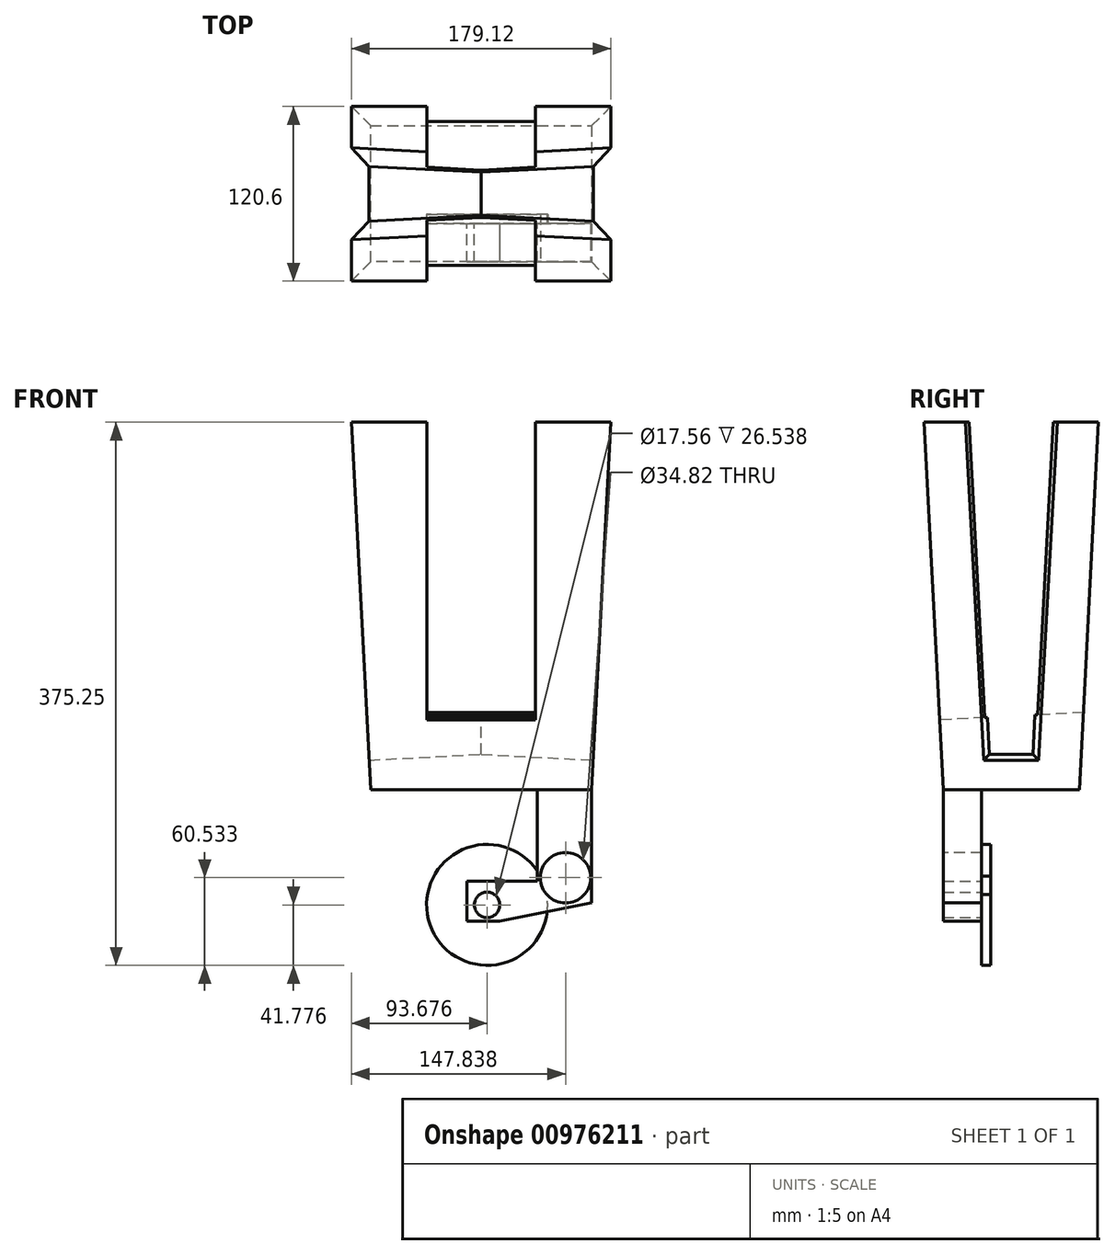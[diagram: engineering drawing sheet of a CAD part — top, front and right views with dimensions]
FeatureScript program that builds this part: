
annotation { "Feature Type Name" : "Feature", "Feature Type Description" : "" }
export const myFeature = defineFeature(function(context is Context, id is Id, definition is map)
    precondition{}
    {
        {
            var Q0;
            Q0=qCreatedBy(makeId("Top.planeOp"),FACE);
            var sketch = newSketch(context, id + "F0", { "sketchPlane" : qUnion([Q0])});
            skLineSegment(sketch, "E0.bottom", {"start": v(76.25, 46.99) * mm, "end": v(-76.25, 46.99) * mm});
            skLineSegment(sketch, "E0.top", {"start": v(76.25, -46.99) * mm, "end": v(-76.25, -46.99) * mm});
            skLineSegment(sketch, "E0.left", {"start": v(76.25, 46.99) * mm, "end": v(76.25, -46.99) * mm});
            skLineSegment(sketch, "E0.right", {"start": v(-76.25, 46.99) * mm, "end": v(-76.25, -46.99) * mm});
            skPoint(sketch, "E0.middle", {"position": v(0, 0) * mm});
            skSolve(sketch);
        }
        {
            var Q0;
            Q0=makeQuery(id+"F0.imprint","IMPRINT",FACE,{"disambiguationData":[TD([[makeQuery(id+"F0.imprint","IMPRINT",EDGE,{"derivedFrom":sQuery(id+"F0.wireOp",EDGE,"E0.bottom")}),1.0]])]});
            extrude(context, id + "F1", {"entities" : qUnion([Q0]), "depth" : 254 * mm, "offsetDistance" : 25.4 * mm, "hasDraft" : true, "draftAngle" : 3 * degree});
        }
        {
            var Q0;
            Q0=qCreatedBy(makeId("Right.planeOp"),FACE);
            var sketch = newSketch(context, id + "F2", { "sketchPlane" : qUnion([Q0])});
            skLineSegment(sketch, "E1", {"start": v(-27.04, 254.5) * mm, "end": v(-14.99, 24.56) * mm});
            skLineSegment(sketch, "E2", {"start": v(-14.99, 24.56) * mm, "end": v(0, 24.56) * mm});
            skLineSegment(sketch, "E3.MirrorCS", {"start": v(27.04, 254.5) * mm, "end": v(14.99, 24.56) * mm});
            skLineSegment(sketch, "E4.MirrorCS", {"start": v(14.99, 24.56) * mm, "end": v(0, 24.56) * mm});
            skLineSegment(sketch, "E5", {"start": v(-27.04, 254.5) * mm, "end": v(27.04, 254.5) * mm});
            skSolve(sketch);
        }
        {
            var Q0;
            Q0 = qSketchRegion(id + "F2", true);
            extrude(context, id + "F3", {"entities" : qUnion([Q0]), "operationType" : NewBodyOperationType.REMOVE, "oppositeDirection" : true, "depth" : 140.97 * mm, "offsetDistance" : 25.4 * mm, "hasDraft" : true, "draftAngle" : 3 * degree, "hasSecondDirection" : true, "secondDirectionOppositeDirection" : false, "secondDirectionDepth" : 247.14 * mm, "hasSecondDirectionDraft" : true, "secondDirectionDraftAngle" : 3 * degree});
        }
        {
            var Q0;
            Q0=makeQuery(id+"F1.opExtrude","SWEPT_FACE",FACE,{"disambiguationData":[OSD([sQuery(id+"F0.wireOp",EDGE,"E0.top")])]});
            var sketch = newSketch(context, id + "F4", { "sketchPlane" : qUnion([Q0])});
            skLineSegment(sketch, "E6", {"start": v(-37.38, 256.8) * mm, "end": v(-37.38, 50.78) * mm});
            skLineSegment(sketch, "E7", {"start": v(-37.38, 50.78) * mm, "end": v(0, 50.78) * mm});
            skLineSegment(sketch, "E8", {"start": v(0, 50.78) * mm, "end": v(0, 256.8) * mm});
            skLineSegment(sketch, "E9", {"start": v(0, 256.8) * mm, "end": v(-37.38, 256.8) * mm});
            skLineSegment(sketch, "E10.MirrorCS", {"start": v(0, 256.8) * mm, "end": v(37.38, 256.8) * mm});
            skLineSegment(sketch, "E11.MirrorCS", {"start": v(37.38, 256.8) * mm, "end": v(37.38, 50.78) * mm});
            skLineSegment(sketch, "E12.MirrorCS", {"start": v(37.38, 50.78) * mm, "end": v(0, 50.78) * mm});
            skSolve(sketch);
        }
        {
            var Q0;
            Q0 = qSketchRegion(id + "F4", true);
            extrude(context, id + "F5", {"entities" : qUnion([Q0]), "operationType" : NewBodyOperationType.REMOVE, "oppositeDirection" : true, "depth" : 149.86 * mm, "offsetDistance" : 25.4 * mm});
        }
        {
            var Q0;
            Q0=makeQuery(id+"F1.opExtrude","CAP_FACE",FACE,{"disambiguationData":[OSD([sQuery(id+"F0.wireOp",EDGE,"E0.bottom"),sQuery(id+"F0.wireOp",EDGE,"E0.top"),sQuery(id+"F0.wireOp",EDGE,"E0.left"),sQuery(id+"F0.wireOp",EDGE,"E0.right")])],"isStart":true});
            var sketch = newSketch(context, id + "F6", { "sketchPlane" : qUnion([Q0])});
            skLineSegment(sketch, "E13.bottom", {"start": v(76.25, 46.99) * mm, "end": v(38.68, 46.99) * mm});
            skLineSegment(sketch, "E13.top", {"start": v(76.25, 20.45) * mm, "end": v(38.68, 20.45) * mm});
            skLineSegment(sketch, "E13.left", {"start": v(76.25, 46.99) * mm, "end": v(76.25, 20.45) * mm});
            skLineSegment(sketch, "E13.right", {"start": v(38.68, 46.99) * mm, "end": v(38.68, 20.45) * mm});
            skSolve(sketch);
        }
        {
            var Q0;
            Q0 = qSketchRegion(id + "F6", true);
            extrude(context, id + "F7", {"entities" : qUnion([Q0]), "operationType" : NewBodyOperationType.ADD, "depth" : 90.68 * mm, "offsetDistance" : 25.4 * mm});
        }
        {
            var Q0;
            Q0=makeQuery(id+"F7.opExtrude","SWEPT_FACE",FACE,{"disambiguationData":[OSD([sQuery(id+"F6.wireOp",EDGE,"E13.right")])]});
            var sketch = newSketch(context, id + "F8", { "sketchPlane" : qUnion([Q0])});
            skLineSegment(sketch, "E14.bottom", {"start": v(46.99, -90.68) * mm, "end": v(20.45, -90.68) * mm});
            skLineSegment(sketch, "E14.top", {"start": v(46.99, -63) * mm, "end": v(20.45, -63) * mm});
            skLineSegment(sketch, "E14.left", {"start": v(46.99, -90.68) * mm, "end": v(46.99, -63) * mm});
            skLineSegment(sketch, "E14.right", {"start": v(20.45, -90.68) * mm, "end": v(20.45, -63) * mm});
            skSolve(sketch);
        }
        {
            var Q0;
            Q0 = qSketchRegion(id + "F8", true);
            extrude(context, id + "F9", {"entities" : qUnion([Q0]), "operationType" : NewBodyOperationType.ADD, "depth" : 48.5 * mm, "offsetDistance" : 25.4 * mm});
        }
        {
            var Q0;
            Q0=makeQuery(id+"F9.boolean.opBoolean","MERGE",FACE,{"derivedFrom":[makeQuery(id+"F7.opExtrude","SWEPT_FACE",FACE,{"disambiguationData":[OSD([sQuery(id+"F6.wireOp",EDGE,"E13.top")])]}),makeQuery(id+"F9.opExtrude","SWEPT_FACE",FACE,{"disambiguationData":[OSD([sQuery(id+"F8.wireOp",EDGE,"E14.right")])]})]});
            var sketch = newSketch(context, id + "F10", { "sketchPlane" : qUnion([Q0])});
            skCircle(sketch, "E15", {"center": v(-4.12, -79.47) * mm, "radius": 8.78 * mm});
            skSolve(sketch);
        }
        {
            var Q0;
            Q0 = qSketchRegion(id + "F10", true);
            extrude(context, id + "F11", {"entities" : qUnion([Q0]), "operationType" : NewBodyOperationType.REMOVE, "oppositeDirection" : true, "depth" : 38.35 * mm, "offsetDistance" : 25.4 * mm});
        }
        {
            var Q0;
            Q0=makeQuery(id+"F9.boolean.opBoolean","MERGE",FACE,{"derivedFrom":[makeQuery(id+"F7.opExtrude","SWEPT_FACE",FACE,{"disambiguationData":[OSD([sQuery(id+"F6.wireOp",EDGE,"E13.top")])]}),makeQuery(id+"F9.opExtrude","SWEPT_FACE",FACE,{"disambiguationData":[OSD([sQuery(id+"F8.wireOp",EDGE,"E14.right")])]})]});
            var sketch = newSketch(context, id + "F12", { "sketchPlane" : qUnion([Q0])});
            skCircle(sketch, "E16", {"center": v(-4.12, -79.47) * mm, "radius": 41.78 * mm});
            skSolve(sketch);
        }
        {
            var Q0;
            Q0 = qSketchRegion(id + "F12", true);
            extrude(context, id + "F13", {"entities" : qUnion([Q0]), "operationType" : NewBodyOperationType.ADD, "depth" : 6.35 * mm, "offsetDistance" : 25.4 * mm});
        }
        {
            var Q0;
            Q0=makeQuery(id+"F7.opExtrude","CAP_EDGE",EDGE,{"disambiguationData":[OSD([sQuery(id+"F6.wireOp",EDGE,"E13.left")])],"isStart":false});
            chamfer(context, id + "F14", {"entities" : qUnion([Q0]), "chamferType" : ChamferType.TWO_OFFSETS, "width1" : 63.5 * mm, "oppositeDirection" : false, "width2" : 12.7 * mm, "tangentPropagation" : true});
        }
        {
            var Q0;
            Q0=makeQuery(id+"F9.boolean.opBoolean","MERGE",FACE,{"derivedFrom":[makeQuery(id+"F7.opExtrude","SWEPT_FACE",FACE,{"disambiguationData":[OSD([sQuery(id+"F6.wireOp",EDGE,"E13.bottom")])]}),makeQuery(id+"F9.opExtrude","SWEPT_FACE",FACE,{"disambiguationData":[OSD([sQuery(id+"F8.wireOp",EDGE,"E14.left")])]})]});
            var sketch = newSketch(context, id + "F15", { "sketchPlane" : qUnion([Q0])});
            skCircle(sketch, "E17", {"center": v(58.28, -60.72) * mm, "radius": 17.41 * mm});
            skSolve(sketch);
        }
        {
            var Q0;
            Q0 = qSketchRegion(id + "F15", true);
            extrude(context, id + "F16", {"entities" : qUnion([Q0]), "operationType" : NewBodyOperationType.REMOVE, "oppositeDirection" : true, "depth" : 87.38 * mm, "offsetDistance" : 25.4 * mm});
        }
    });
